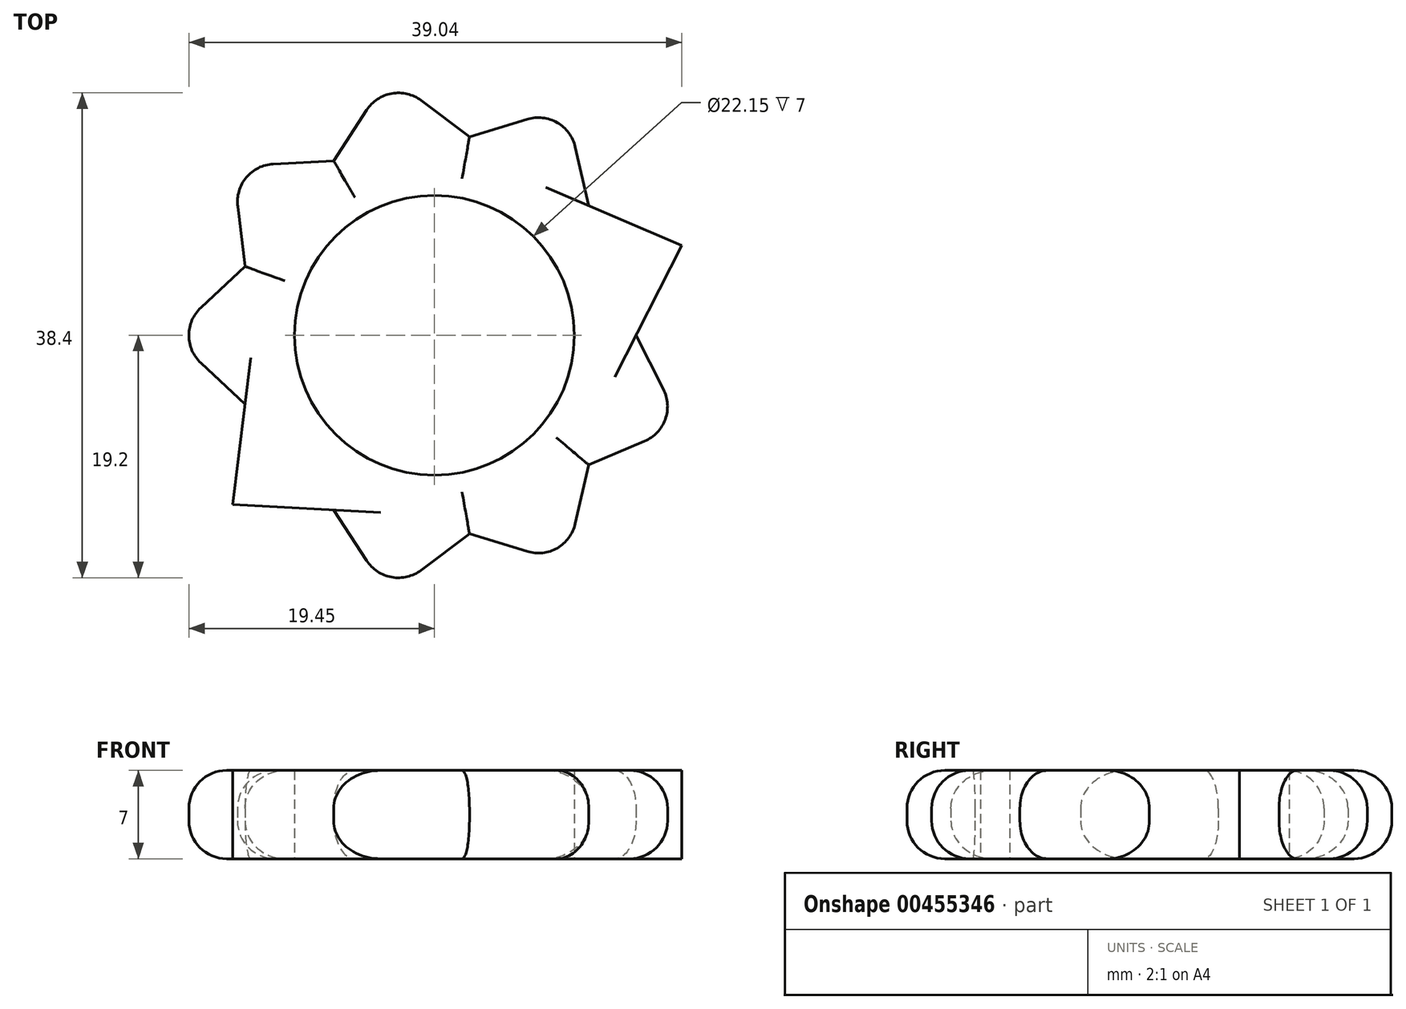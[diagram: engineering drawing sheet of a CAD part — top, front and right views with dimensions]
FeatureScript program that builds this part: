
annotation { "Feature Type Name" : "Feature", "Feature Type Description" : "" }
export const myFeature = defineFeature(function(context is Context, id is Id, definition is map)
    precondition{}
    {
        {
            var Q0;
            Q0=qCreatedBy(makeId("Top.planeOp"),FACE);
            var sketch = newSketch(context, id + "F0", { "sketchPlane" : qUnion([Q0])});
            skCircle(sketch, "E0", {"center": v(0, 0) * mm, "radius": 11.07 * mm});
            skCircle(sketch, "E1", {"center": v(0, 0) * mm, "radius": 15 * mm});
            skCircle(sketch, "E2.cCircle", {"center": v(0, 0) * mm, "radius": 15 * mm, "construction": true});
            skLineSegment(sketch, "E2.0", {"start": v(-15, -5.46) * mm, "end": v(-15, 5.46) * mm});
            skLineSegment(sketch, "E2.1", {"start": v(-15, 5.46) * mm, "end": v(-7.98, 13.82) * mm});
            skLineSegment(sketch, "E2.2", {"start": v(-7.98, 13.82) * mm, "end": v(2.77, 15.72) * mm});
            skLineSegment(sketch, "E2.3", {"start": v(2.77, 15.72) * mm, "end": v(12.23, 10.26) * mm});
            skLineSegment(sketch, "E2.4", {"start": v(12.23, 10.26) * mm, "end": v(15.96, 0) * mm});
            skLineSegment(sketch, "E2.5", {"start": v(15.96, 0) * mm, "end": v(12.23, -10.26) * mm});
            skLineSegment(sketch, "E2.6", {"start": v(12.23, -10.26) * mm, "end": v(2.77, -15.72) * mm});
            skLineSegment(sketch, "E2.7", {"start": v(2.77, -15.72) * mm, "end": v(-7.98, -13.82) * mm});
            skLineSegment(sketch, "E2.8", {"start": v(-7.98, -13.82) * mm, "end": v(-15, -5.46) * mm});
            skPoint(sketch, "E2.0.midPoint", {"position": v(-15, 0) * mm});
            skLineSegment(sketch, "E3", {"start": v(-15, 5.46) * mm, "end": v(-15.58, 10.21) * mm});
            skLineSegment(sketch, "E4.MirrorCS", {"start": v(-7.98, 13.82) * mm, "end": v(-12.76, 13.57) * mm});
            skLineSegment(sketch, "E5.MirrorCS", {"start": v(12.23, 10.26) * mm, "end": v(19.59, 7.13) * mm});
            skLineSegment(sketch, "E6.MirrorCS", {"start": v(15.96, 0) * mm, "end": v(19.59, 7.13) * mm});
            skLineSegment(sketch, "E7.MirrorCS", {"start": v(15.96, 0) * mm, "end": v(18.13, -4.27) * mm});
            skLineSegment(sketch, "E8.MirrorCS", {"start": v(12.23, -10.26) * mm, "end": v(16.63, -8.39) * mm});
            skLineSegment(sketch, "E9.MirrorCS", {"start": v(-15, 5.46) * mm, "end": v(-18.5, 2.2) * mm});
            skLineSegment(sketch, "E10.MirrorCS", {"start": v(-15, -5.46) * mm, "end": v(-18.5, -2.2) * mm});
            skLineSegment(sketch, "E11.MirrorCS", {"start": v(-7.98, -13.82) * mm, "end": v(-15.97, -13.4) * mm});
            skLineSegment(sketch, "E12.MirrorCS", {"start": v(-15, -5.46) * mm, "end": v(-15.97, -13.4) * mm});
            skLineSegment(sketch, "E13.MirrorCS", {"start": v(2.77, 15.72) * mm, "end": v(7.35, 17.11) * mm});
            skLineSegment(sketch, "E14.MirrorCS", {"start": v(12.23, 10.26) * mm, "end": v(11.15, 14.92) * mm});
            skLineSegment(sketch, "E15.MirrorCS", {"start": v(-7.98, 13.82) * mm, "end": v(-3.62, 20.53) * mm});
            skLineSegment(sketch, "E16.MirrorCS", {"start": v(2.77, 15.72) * mm, "end": v(-3.62, 20.53) * mm});
            skLineSegment(sketch, "E17.MirrorCS", {"start": v(-7.98, -13.82) * mm, "end": v(-3.62, -20.53) * mm});
            skLineSegment(sketch, "E18.MirrorCS", {"start": v(2.77, -15.72) * mm, "end": v(-3.62, -20.53) * mm});
            skLineSegment(sketch, "E19.MirrorCS", {"start": v(2.77, -15.72) * mm, "end": v(7.35, -17.11) * mm});
            skLineSegment(sketch, "E20.MirrorCS", {"start": v(12.23, -10.26) * mm, "end": v(11.15, -14.92) * mm});
            skPoint(sketch, "E21.visualSharp", {"position": v(-15.97, 13.4) * mm});
            skArc(sketch, "E21.filletArc", {"start": v(-12.76, 13.57) * mm, "mid": v(-14.9, 12.5) * mm, "end": v(-15.58, 10.21) * mm});
            skPoint(sketch, "E22.visualSharp", {"position": v(10.42, -18.05) * mm});
            skArc(sketch, "E22.filletArc", {"start": v(7.35, -17.11) * mm, "mid": v(9.72, -16.84) * mm, "end": v(11.15, -14.92) * mm});
            skPoint(sketch, "E23.visualSharp", {"position": v(19.59, -7.13) * mm});
            skArc(sketch, "E23.filletArc", {"start": v(16.63, -8.39) * mm, "mid": v(18.28, -6.65) * mm, "end": v(18.13, -4.27) * mm});
            skPoint(sketch, "E24.visualSharp", {"position": v(10.42, 18.05) * mm});
            skArc(sketch, "E24.filletArc", {"start": v(11.15, 14.92) * mm, "mid": v(9.72, 16.84) * mm, "end": v(7.35, 17.11) * mm});
            skPoint(sketch, "E25.visualSharp", {"position": v(-20.84, 0) * mm});
            skArc(sketch, "E25.filletArc", {"start": v(-18.5, 2.2) * mm, "mid": v(-19.45, 0) * mm, "end": v(-18.5, -2.2) * mm});
            skSolve(sketch);
        }
        {
            var Q0;
            Q0 = qSketchRegion(id + "F0", true);
            var Q1;
            Q1=makeQuery(id+"F0.imprint","IMPRINT",FACE,{"disambiguationData":[TD([[makeQuery(id+"F0.imprint","IMPRINT",EDGE,{"derivedFrom":sQuery(id+"F0.wireOp",EDGE,"E0")}),-1.0]])]});
            extrude(context, id + "F1", {"entities" : qUnion([Q0, Q1]), "depth" : 7 * mm, "offsetDistance" : 25 * mm});
        }
        {
            var Q0;
            Q0=makeQuery(id+"F1.opExtrude","CAP_EDGE",EDGE,{"disambiguationData":[OSD([sQuery(id+"F0.wireOp",EDGE,"E15.MirrorCS")])],"isStart":false});
            var Q1;
            Q1=makeQuery(id+"F1.opExtrude","CAP_EDGE",EDGE,{"disambiguationData":[OSD([sQuery(id+"F0.wireOp",EDGE,"E16.MirrorCS")])],"isStart":false});
            var Q2;
            Q2=makeQuery(id+"F1.opExtrude","CAP_EDGE",EDGE,{"disambiguationData":[OSD([sQuery(id+"F0.wireOp",EDGE,"E16.MirrorCS")])],"isStart":true});
            var Q3;
            Q3=makeQuery(id+"F1.opExtrude","CAP_EDGE",EDGE,{"disambiguationData":[OSD([sQuery(id+"F0.wireOp",EDGE,"E4.MirrorCS")])],"isStart":false});
            var Q4;
            Q4=makeQuery(id+"F1.opExtrude","CAP_EDGE",EDGE,{"disambiguationData":[OSD([sQuery(id+"F0.wireOp",EDGE,"E9.MirrorCS")])],"isStart":false});
            var Q5;
            Q5=makeQuery(id+"F1.opExtrude","CAP_EDGE",EDGE,{"disambiguationData":[OSD([sQuery(id+"F0.wireOp",EDGE,"E10.MirrorCS")])],"isStart":false});
            var Q6;
            Q6=makeQuery(id+"F1.opExtrude","CAP_EDGE",EDGE,{"disambiguationData":[OSD([sQuery(id+"F0.wireOp",EDGE,"E9.MirrorCS")])],"isStart":true});
            var Q7;
            Q7=makeQuery(id+"F1.opExtrude","CAP_EDGE",EDGE,{"disambiguationData":[OSD([sQuery(id+"F0.wireOp",EDGE,"E10.MirrorCS")])],"isStart":true});
            var Q8;
            Q8=makeQuery(id+"F1.opExtrude","CAP_EDGE",EDGE,{"disambiguationData":[OSD([sQuery(id+"F0.wireOp",EDGE,"E12.MirrorCS")])],"isStart":false});
            var Q9;
            Q9=makeQuery(id+"F1.opExtrude","CAP_EDGE",EDGE,{"disambiguationData":[OSD([sQuery(id+"F0.wireOp",EDGE,"E17.MirrorCS")])],"isStart":false});
            var Q10;
            Q10=makeQuery(id+"F1.opExtrude","CAP_EDGE",EDGE,{"disambiguationData":[OSD([sQuery(id+"F0.wireOp",EDGE,"E11.MirrorCS")])],"isStart":false});
            var Q11;
            Q11=makeQuery(id+"F1.opExtrude","CAP_EDGE",EDGE,{"disambiguationData":[OSD([sQuery(id+"F0.wireOp",EDGE,"E18.MirrorCS")])],"isStart":false});
            var Q12;
            Q12=makeQuery(id+"F1.opExtrude","CAP_EDGE",EDGE,{"disambiguationData":[OSD([sQuery(id+"F0.wireOp",EDGE,"E19.MirrorCS")])],"isStart":false});
            var Q13;
            Q13=makeQuery(id+"F1.opExtrude","CAP_EDGE",EDGE,{"disambiguationData":[OSD([sQuery(id+"F0.wireOp",EDGE,"E20.MirrorCS")])],"isStart":false});
            var Q14;
            Q14=makeQuery(id+"F1.opExtrude","CAP_EDGE",EDGE,{"disambiguationData":[OSD([sQuery(id+"F0.wireOp",EDGE,"E8.MirrorCS")])],"isStart":false});
            var Q15;
            Q15=makeQuery(id+"F1.opExtrude","CAP_EDGE",EDGE,{"disambiguationData":[OSD([sQuery(id+"F0.wireOp",EDGE,"E6.MirrorCS")])],"isStart":false});
            var Q16;
            Q16=makeQuery(id+"F1.opExtrude","CAP_EDGE",EDGE,{"disambiguationData":[OSD([sQuery(id+"F0.wireOp",EDGE,"E14.MirrorCS")])],"isStart":false});
            var Q17;
            Q17=makeQuery(id+"F1.opExtrude","CAP_EDGE",EDGE,{"disambiguationData":[OSD([sQuery(id+"F0.wireOp",EDGE,"E7.MirrorCS")])],"isStart":false});
            var Q18;
            Q18=makeQuery(id+"F1.opExtrude","CAP_EDGE",EDGE,{"disambiguationData":[OSD([sQuery(id+"F0.wireOp",EDGE,"E13.MirrorCS")])],"isStart":false});
            var Q19;
            Q19=makeQuery(id+"F1.opExtrude","CAP_EDGE",EDGE,{"disambiguationData":[OSD([sQuery(id+"F0.wireOp",EDGE,"E5.MirrorCS")])],"isStart":false});
            var Q20;
            Q20=makeQuery(id+"F1.opExtrude","CAP_EDGE",EDGE,{"disambiguationData":[OSD([sQuery(id+"F0.wireOp",EDGE,"E3")])],"isStart":false});
            var Q21;
            Q21=makeQuery(id+"F1.opExtrude","CAP_EDGE",EDGE,{"disambiguationData":[OSD([sQuery(id+"F0.wireOp",EDGE,"E6.MirrorCS")])],"isStart":true});
            var Q22;
            Q22=makeQuery(id+"F1.opExtrude","SWEPT_EDGE",EDGE,{"disambiguationData":[OSD([sQuery(id+"F0.wireOp",EDGE,"E6.MirrorCS"),sQuery(id+"F0.wireOp",EDGE,"E5.MirrorCS")])]});
            var Q23;
            Q23=makeQuery(id+"F1.opExtrude","CAP_EDGE",EDGE,{"disambiguationData":[OSD([sQuery(id+"F0.wireOp",EDGE,"E8.MirrorCS")])],"isStart":true});
            var Q24;
            Q24=makeQuery(id+"F1.opExtrude","CAP_EDGE",EDGE,{"disambiguationData":[OSD([sQuery(id+"F0.wireOp",EDGE,"E20.MirrorCS")])],"isStart":true});
            var Q25;
            Q25=makeQuery(id+"F1.opExtrude","CAP_EDGE",EDGE,{"disambiguationData":[OSD([sQuery(id+"F0.wireOp",EDGE,"E19.MirrorCS")])],"isStart":true});
            var Q26;
            Q26=makeQuery(id+"F1.opExtrude","CAP_EDGE",EDGE,{"disambiguationData":[OSD([sQuery(id+"F0.wireOp",EDGE,"E17.MirrorCS")])],"isStart":true});
            var Q27;
            Q27=makeQuery(id+"F1.opExtrude","CAP_EDGE",EDGE,{"disambiguationData":[OSD([sQuery(id+"F0.wireOp",EDGE,"E12.MirrorCS")])],"isStart":true});
            var Q28;
            Q28=makeQuery(id+"F1.opExtrude","CAP_EDGE",EDGE,{"disambiguationData":[OSD([sQuery(id+"F0.wireOp",EDGE,"E3")])],"isStart":true});
            var Q29;
            Q29=makeQuery(id+"F1.opExtrude","CAP_EDGE",EDGE,{"disambiguationData":[OSD([sQuery(id+"F0.wireOp",EDGE,"E4.MirrorCS")])],"isStart":true});
            var Q30;
            Q30=makeQuery(id+"F1.opExtrude","CAP_EDGE",EDGE,{"disambiguationData":[OSD([sQuery(id+"F0.wireOp",EDGE,"E14.MirrorCS")])],"isStart":true});
            var Q31;
            Q31=makeQuery(id+"F1.opExtrude","CAP_EDGE",EDGE,{"disambiguationData":[OSD([sQuery(id+"F0.wireOp",EDGE,"E15.MirrorCS")])],"isStart":true});
            var Q32;
            Q32=makeQuery(id+"F1.opExtrude","CAP_EDGE",EDGE,{"disambiguationData":[OSD([sQuery(id+"F0.wireOp",EDGE,"E11.MirrorCS")])],"isStart":true});
            var Q33;
            Q33=makeQuery(id+"F1.opExtrude","CAP_EDGE",EDGE,{"disambiguationData":[OSD([sQuery(id+"F0.wireOp",EDGE,"E18.MirrorCS")])],"isStart":true});
            var Q34;
            Q34=makeQuery(id+"F1.opExtrude","CAP_EDGE",EDGE,{"disambiguationData":[OSD([sQuery(id+"F0.wireOp",EDGE,"E7.MirrorCS")])],"isStart":true});
            fillet(context, id + "F2", {"entities" : qUnion([Q0, Q1, Q2, Q3, Q4, Q5, Q6, Q7, Q8, Q9, Q10, Q11, Q12, Q13, Q14, Q15, Q16, Q17, Q18, Q19, Q20, Q21, Q22, Q23, Q24, Q25, Q26, Q27, Q28, Q29, Q30, Q31, Q32, Q33, Q34]), "radius" : 3 * mm, "tangentPropagation" : true, "allowEdgeOverflow" : false});
        }
        {
            var Q0;
            Q0=makeQuery(id+"F1.opExtrude","CAP_EDGE",EDGE,{"disambiguationData":[OSD([sQuery(id+"F0.wireOp",EDGE,"E5.MirrorCS")])],"isStart":true});
            var Q1;
            Q1=makeQuery(id+"F2.opFillet","BLEND_EDGE",EDGE,{"blendedFrom":[makeQuery(id+"F1.opExtrude","CAP_EDGE",EDGE,{"disambiguationData":[OSD([sQuery(id+"F0.wireOp",EDGE,"E18.MirrorCS")])],"isStart":false}),makeQuery(id+"F1.opExtrude","CAP_EDGE",EDGE,{"disambiguationData":[OSD([sQuery(id+"F0.wireOp",EDGE,"E17.MirrorCS")])],"isStart":false})],"blendedInto":[]});
            var Q2;
            Q2=makeQuery(id+"F2.opFillet","BLEND_EDGE",EDGE,{"blendedFrom":[makeQuery(id+"F1.opExtrude","CAP_EDGE",EDGE,{"disambiguationData":[OSD([sQuery(id+"F0.wireOp",EDGE,"E11.MirrorCS")])],"isStart":true}),makeQuery(id+"F1.opExtrude","CAP_EDGE",EDGE,{"disambiguationData":[OSD([sQuery(id+"F0.wireOp",EDGE,"E12.MirrorCS")])],"isStart":true})],"blendedInto":[]});
            var Q3;
            Q3=makeQuery(id+"F2.opFillet","BLEND_EDGE",EDGE,{"blendedFrom":[makeQuery(id+"F1.opExtrude","CAP_EDGE",EDGE,{"disambiguationData":[OSD([sQuery(id+"F0.wireOp",EDGE,"E15.MirrorCS")])],"isStart":true}),makeQuery(id+"F1.opExtrude","CAP_EDGE",EDGE,{"disambiguationData":[OSD([sQuery(id+"F0.wireOp",EDGE,"E16.MirrorCS")])],"isStart":true})],"blendedInto":[]});
            fillet(context, id + "F3", {"entities" : qUnion([Q0, Q1, Q2, Q3]), "radius" : 3 * mm, "tangentPropagation" : true, "allowEdgeOverflow" : false});
        }
    });
